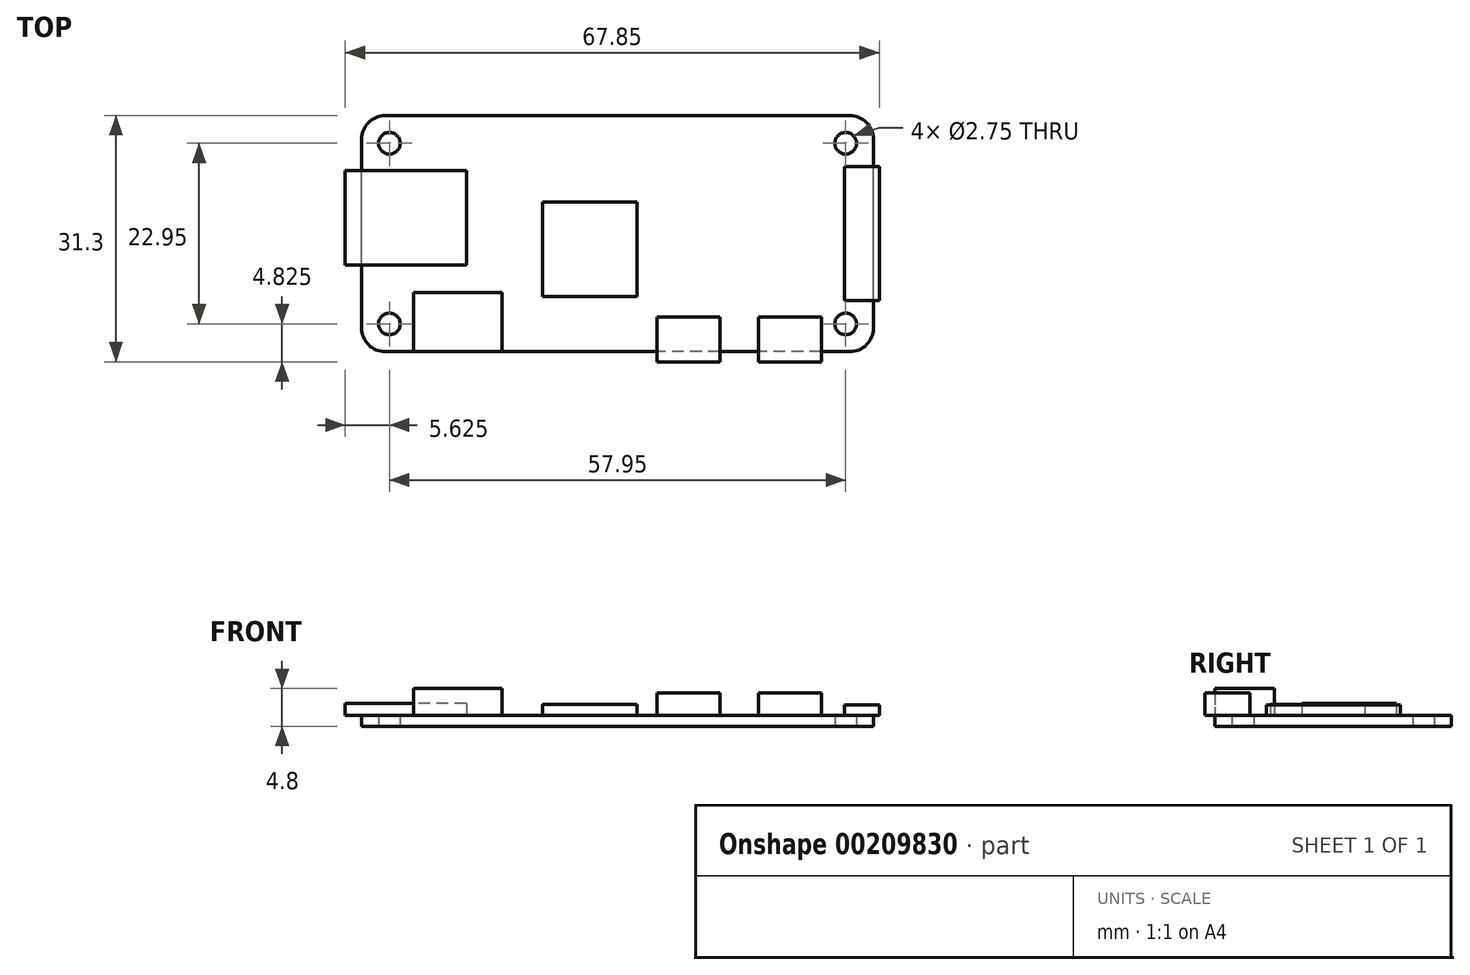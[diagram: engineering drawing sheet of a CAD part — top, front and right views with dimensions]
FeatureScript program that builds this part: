
annotation { "Feature Type Name" : "Feature", "Feature Type Description" : "" }
export const myFeature = defineFeature(function(context is Context, id is Id, definition is map)
    precondition{}
    {
        {
            var Q0;
            Q0=qCreatedBy(makeId("Top.planeOp"),FACE);
            var sketch = newSketch(context, id + "F0", { "sketchPlane" : qUnion([Q0])});
            skLineSegment(sketch, "E0.bottom", {"start": v(29.5, -15) * mm, "end": v(-29.5, -15) * mm});
            skLineSegment(sketch, "E0.top", {"start": v(29.5, 15) * mm, "end": v(-29.5, 15) * mm});
            skLineSegment(sketch, "E0.left", {"start": v(32.5, -12) * mm, "end": v(32.5, 12) * mm});
            skLineSegment(sketch, "E0.right", {"start": v(-32.5, -12) * mm, "end": v(-32.5, 12) * mm});
            skPoint(sketch, "E0.middle", {"position": v(0, 0) * mm});
            skCircle(sketch, "E1", {"center": v(-28.98, 11.47) * mm, "radius": 1.38 * mm});
            skCircle(sketch, "E2", {"center": v(28.98, 11.47) * mm, "radius": 1.38 * mm});
            skCircle(sketch, "E3", {"center": v(-28.98, -11.47) * mm, "radius": 1.38 * mm});
            skCircle(sketch, "E4", {"center": v(28.98, -11.47) * mm, "radius": 1.38 * mm});
            skPoint(sketch, "E5.visualSharp", {"position": v(-32.5, 15) * mm});
            skArc(sketch, "E5.filletArc", {"start": v(-29.5, 15) * mm, "mid": v(-31.62, 14.12) * mm, "end": v(-32.5, 12) * mm});
            skPoint(sketch, "E6.visualSharp", {"position": v(32.5, 15) * mm});
            skArc(sketch, "E6.filletArc", {"start": v(32.5, 12) * mm, "mid": v(31.62, 14.12) * mm, "end": v(29.5, 15) * mm});
            skPoint(sketch, "E7.visualSharp", {"position": v(32.5, -15) * mm});
            skArc(sketch, "E7.filletArc", {"start": v(29.5, -15) * mm, "mid": v(31.62, -14.12) * mm, "end": v(32.5, -12) * mm});
            skPoint(sketch, "E8.visualSharp", {"position": v(-32.5, -15) * mm});
            skArc(sketch, "E8.filletArc", {"start": v(-32.5, -12) * mm, "mid": v(-31.62, -14.12) * mm, "end": v(-29.5, -15) * mm});
            skSolve(sketch);
        }
        {
            var Q0;
            Q0=qSketchRegion(id+"F0",true);
            extrude(context, id + "F1", {"entities" : qUnion([Q0]), "depth" : 1.4 * mm});
        }
        {
            var Q0;
            Q0=makeQuery(id+"F1.opExtrude","CAP_FACE",FACE,{"disambiguationData":[OSD([sQuery(id+"F0.wireOp",EDGE,"E0.bottom"),sQuery(id+"F0.wireOp",EDGE,"E0.top"),sQuery(id+"F0.wireOp",EDGE,"E0.left"),sQuery(id+"F0.wireOp",EDGE,"E0.right"),sQuery(id+"F0.wireOp",EDGE,"E1"),sQuery(id+"F0.wireOp",EDGE,"E2"),sQuery(id+"F0.wireOp",EDGE,"E3"),sQuery(id+"F0.wireOp",EDGE,"E4"),sQuery(id+"F0.wireOp",EDGE,"E5.filletArc"),sQuery(id+"F0.wireOp",EDGE,"E6.filletArc"),sQuery(id+"F0.wireOp",EDGE,"E7.filletArc"),sQuery(id+"F0.wireOp",EDGE,"E8.filletArc")])],"isStart":false});
            var sketch = newSketch(context, id + "F2", { "sketchPlane" : qUnion([Q0])});
            skLineSegment(sketch, "E9.bottom", {"start": v(2.5, -8) * mm, "end": v(-9.5, -8) * mm});
            skLineSegment(sketch, "E9.top", {"start": v(2.5, 4) * mm, "end": v(-9.5, 4) * mm});
            skLineSegment(sketch, "E9.left", {"start": v(2.5, -8) * mm, "end": v(2.5, 4) * mm});
            skLineSegment(sketch, "E9.right", {"start": v(-9.5, -8) * mm, "end": v(-9.5, 4) * mm});
            skPoint(sketch, "E9.middle", {"position": v(-3.5, -2) * mm});
            skLineSegment(sketch, "E10.bottom", {"start": v(33.25, -8.5) * mm, "end": v(28.85, -8.5) * mm});
            skLineSegment(sketch, "E10.top", {"start": v(33.25, 8.5) * mm, "end": v(28.85, 8.5) * mm});
            skLineSegment(sketch, "E10.left", {"start": v(33.25, -8.5) * mm, "end": v(33.25, 8.5) * mm});
            skLineSegment(sketch, "E10.right", {"start": v(28.85, -8.5) * mm, "end": v(28.85, 8.5) * mm});
            skPoint(sketch, "E10.middle", {"position": v(31.05, 0) * mm});
            skPoint(sketch, "E11", {"position": v(32.5, 0) * mm});
            skLineSegment(sketch, "E12.bottom", {"start": v(-19.2, -4) * mm, "end": v(-34.6, -4) * mm});
            skLineSegment(sketch, "E12.top", {"start": v(-19.2, 8) * mm, "end": v(-34.6, 8) * mm});
            skLineSegment(sketch, "E12.left", {"start": v(-19.2, -4) * mm, "end": v(-19.2, 8) * mm});
            skLineSegment(sketch, "E12.right", {"start": v(-34.6, -4) * mm, "end": v(-34.6, 8) * mm});
            skPoint(sketch, "E12.middle", {"position": v(-26.9, 2) * mm});
            skLineSegment(sketch, "E13.bottom", {"start": v(-25.9, -15) * mm, "end": v(-14.7, -15) * mm});
            skLineSegment(sketch, "E13.top", {"start": v(-25.9, -7.5) * mm, "end": v(-14.7, -7.5) * mm});
            skLineSegment(sketch, "E13.left", {"start": v(-25.9, -15) * mm, "end": v(-25.9, -7.5) * mm});
            skLineSegment(sketch, "E13.right", {"start": v(-14.7, -15) * mm, "end": v(-14.7, -7.5) * mm});
            skLineSegment(sketch, "E14.bottom", {"start": v(5, -16.3) * mm, "end": v(13, -16.3) * mm});
            skLineSegment(sketch, "E14.top", {"start": v(5, -10.6) * mm, "end": v(13, -10.6) * mm});
            skLineSegment(sketch, "E14.left", {"start": v(5, -16.3) * mm, "end": v(5, -10.6) * mm});
            skLineSegment(sketch, "E14.right", {"start": v(13, -16.3) * mm, "end": v(13, -10.6) * mm});
            skLineSegment(sketch, "E15.bottom", {"start": v(17.9, -16.3) * mm, "end": v(25.9, -16.3) * mm});
            skLineSegment(sketch, "E15.top", {"start": v(17.9, -10.6) * mm, "end": v(25.9, -10.6) * mm});
            skLineSegment(sketch, "E15.left", {"start": v(17.9, -16.3) * mm, "end": v(17.9, -10.6) * mm});
            skLineSegment(sketch, "E15.right", {"start": v(25.9, -16.3) * mm, "end": v(25.9, -10.6) * mm});
            skSolve(sketch);
        }
        {
            var Q0;
            Q0=makeQuery(id+"F2.imprint","IMPRINT",FACE,{"disambiguationData":[TD([[makeQuery(id+"F2.imprint","IMPRINT",EDGE,{"derivedFrom":sQuery(id+"F2.wireOp",EDGE,"E9.bottom")}),-1.0]])]});
            extrude(context, id + "F3", {"entities" : qUnion([Q0]), "depth" : 1.4 * mm});
        }
        {
            var Q0;
            Q0=makeQuery(id+"F2.imprint","IMPRINT",FACE,{"disambiguationData":[TD([[makeQuery(id+"F2.imprint","IMPRINT",EDGE,{"derivedFrom":sQuery(id+"F2.wireOp",EDGE,"E13.bottom")}),-1.0]])]});
            extrude(context, id + "F4", {"entities" : qUnion([Q0]), "depth" : (4.8 - 1.4) * mm});
        }
        {
            var Q0;
            {var subQ0=sQuery(id+"F2.wireOp",EDGE,"E14.top");Q0=makeQuery(id+"F2.imprint","IMPRINT",FACE,{"disambiguationData":[TD([[makeQuery(id+"F2.imprint","IMPRINT",EDGE,{"derivedFrom":subQ0}),-1.0]])]});}
            var Q1;
            {var subQ0=sQuery(id+"F2.wireOp",EDGE,"E15.top");Q1=makeQuery(id+"F2.imprint","IMPRINT",FACE,{"disambiguationData":[TD([[makeQuery(id+"F2.imprint","IMPRINT",EDGE,{"derivedFrom":subQ0}),-1.0]])]});}
            var Q2;
            {var subQ0=sQuery(id+"F2.wireOp",EDGE,"E15.bottom");Q2=makeQuery(id+"F2.imprint","IMPRINT",FACE,{"disambiguationData":[TD([[makeQuery(id+"F2.imprint","IMPRINT",EDGE,{"derivedFrom":subQ0}),1.0]])]});}
            var Q3;
            {var subQ0=sQuery(id+"F2.wireOp",EDGE,"E14.bottom");Q3=makeQuery(id+"F2.imprint","IMPRINT",FACE,{"disambiguationData":[TD([[makeQuery(id+"F2.imprint","IMPRINT",EDGE,{"derivedFrom":subQ0}),1.0]])]});}
            extrude(context, id + "F5", {"entities" : qUnion([Q0, Q1, Q2, Q3]), "depth" : (4.25 - 1.4) * mm});
        }
        {
            var Q0;
            {var subQ0=sQuery(id+"F2.wireOp",EDGE,"E10.right");Q0=makeQuery(id+"F2.imprint","IMPRINT",FACE,{"disambiguationData":[TD([[makeQuery(id+"F2.imprint","IMPRINT",EDGE,{"derivedFrom":subQ0}),-1.0]])]});}
            var Q1;
            {var subQ0=sQuery(id+"F2.wireOp",EDGE,"E10.left");Q1=makeQuery(id+"F2.imprint","IMPRINT",FACE,{"disambiguationData":[TD([[makeQuery(id+"F2.imprint","IMPRINT",EDGE,{"derivedFrom":subQ0}),1.0]])]});}
            extrude(context, id + "F6", {"entities" : qUnion([Q0, Q1]), "depth" : (2.75 - 1.4) * mm});
        }
        {
            var Q0;
            {var subQ0=sQuery(id+"F2.wireOp",EDGE,"E12.right");Q0=makeQuery(id+"F2.imprint","IMPRINT",FACE,{"disambiguationData":[TD([[makeQuery(id+"F2.imprint","IMPRINT",EDGE,{"derivedFrom":subQ0}),-1.0]])]});}
            var Q1;
            {var subQ0=sQuery(id+"F2.wireOp",EDGE,"E12.left");Q1=makeQuery(id+"F2.imprint","IMPRINT",FACE,{"disambiguationData":[TD([[makeQuery(id+"F2.imprint","IMPRINT",EDGE,{"derivedFrom":subQ0}),1.0]])]});}
            extrude(context, id + "F7", {"entities" : qUnion([Q0, Q1]), "depth" : (2.9 - 1.4) * mm});
        }
    });
